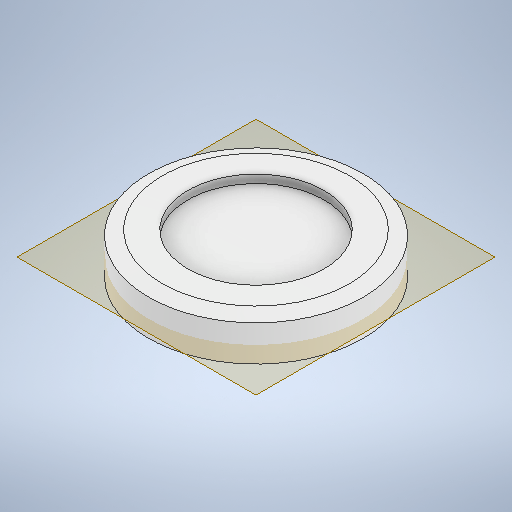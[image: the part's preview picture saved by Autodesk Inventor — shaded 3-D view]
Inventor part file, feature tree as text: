
AUTODESK INVENTOR PART (.ipt)
format: ipt  version: 2025.1 (Build 291241020, 241B)  size: 455,168 bytes
history: native  units: in
note: dims shown in document units (in); Inventor stores cm internally (conversion verified against a paired STEP export)
features: extrude x4, sketch x4, chamfer x2, plane x1, mirror x1
ambient origin geometry x8: Origin, YZ Plane, XZ Plane, XY Plane, X Axis, Y Axis, Z Axis, Center Point
bodies: Solid1 (feature_tree)
feature tree (12):
  extrude  "Extrusion1"  Depth=1.0in
  plane  "Work Plane1"
  extrude  "Extrusion2"  Depth=0.0472in
  extrude  "Extrusion3"  Depth=0.0112in TaperAngle=0.0deg
  extrude  "Extrusion4"  Depth=0.0787in
  chamfer  "Chamfer1"  [1 undecoded]
  chamfer  "Chamfer2"  [1 undecoded]
  sketch  "Sketch1"  dims[d0=1.0in d1=0.0in d2=0.7874in]
  sketch  "Sketch2"  dims[d3=0.0472in d4=0.0in d5=1.2402in]
  sketch  "Sketch3"  dims[d6=0.0in d7=0.0in d8=0.0112in d9=0.0in]
  sketch  "Sketch4"  dims[d10=0.0787in d11=0.0787in d12=0.1374in d13=0.0787in d14=0.0787in d15=0.1374in]
  mirror  "Mirror1"
note: 2 required parameter values undecoded (feature->parameter linkage not recoverable at this tier; creation-order binding heuristic only, values carry confidence <= 0.55)
